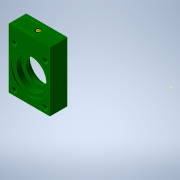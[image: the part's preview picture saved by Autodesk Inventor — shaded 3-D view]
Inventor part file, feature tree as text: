
AUTODESK INVENTOR PART (.ipt)
format: ipt  version: 2020 (Build 240168000, 168)  size: 508,928 bytes
history: native  units: in
note: dims shown in document units (in); Inventor stores cm internally (conversion verified against a paired STEP export)
features: extrude x3, sketch x3, hole x2
ambient origin geometry x8: Origin, YZ Plane, XZ Plane, XY Plane, X Axis, Y Axis, Z Axis, Center Point
bodies: Solid1 (feature_tree)
feature tree (8):
  extrude  "Extrusion1"  Depth=0.4in TaperAngle=0.0deg
  extrude  "Extrusion2"  [1 undecoded]
  sketch  "Sketch3"  dims[d6=0.213in d7=0.75in d8=0.507in d9=0.25in d10=0.5635in d11=0.25in d12=0.8108in d13=0.04in d14=0.75in d15=0.507in d16=0.25in d17=0.5635in d18=1.0in d19=0.8108in]
  extrude  "Extrusion3"  [1 undecoded]
  hole  "Hole1"  [1 undecoded]
  hole  "Hole2"  [1 undecoded]
  sketch  "Sketch1"  dims[d0=0.4in d1=0.0in d2=0.4in d3=0.0in]
  sketch  "Sketch2"  dims[d4=0.6in d5=0.0in]
note: 4 required parameter values undecoded (feature->parameter linkage not recoverable at this tier; creation-order binding heuristic only, values carry confidence <= 0.55)
